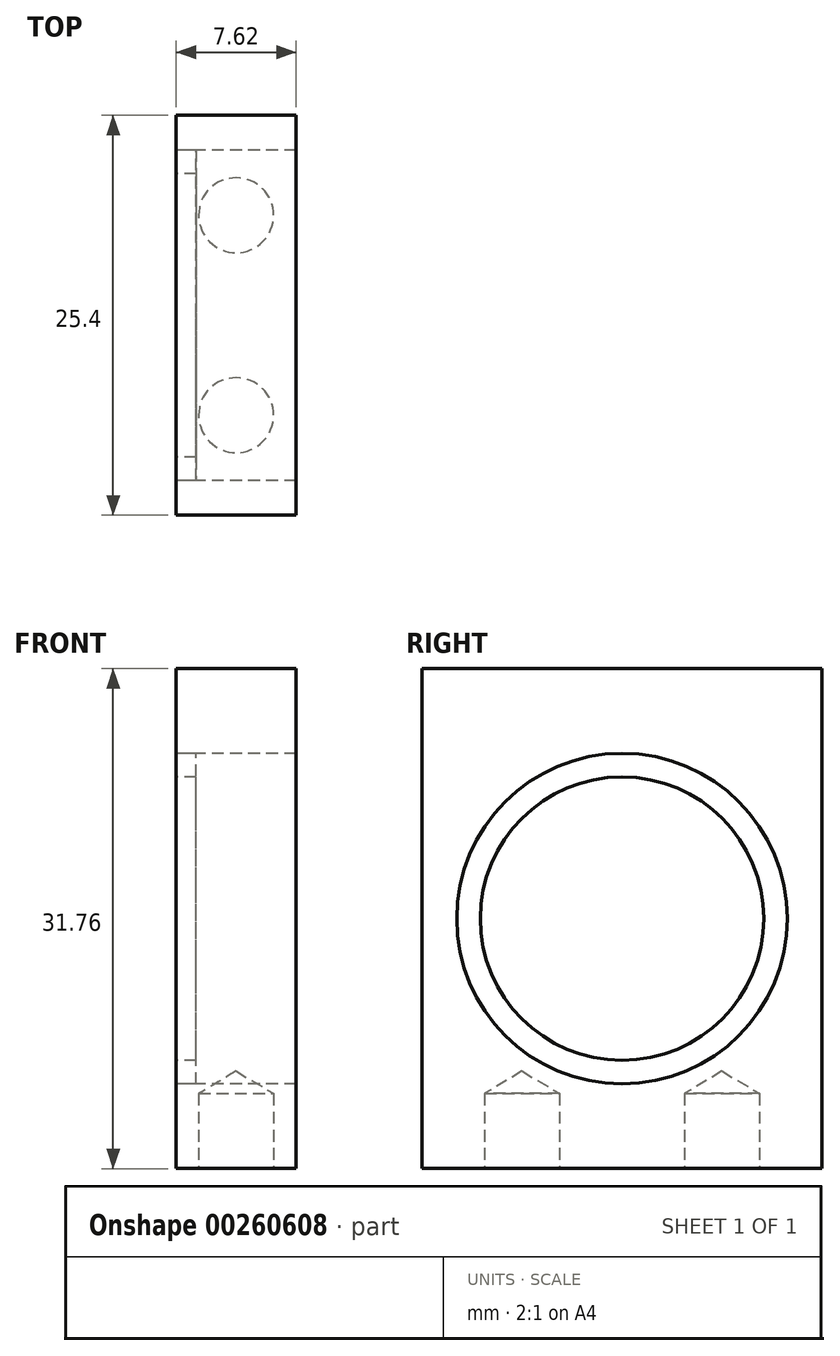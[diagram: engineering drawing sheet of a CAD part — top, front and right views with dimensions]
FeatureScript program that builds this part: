
annotation { "Feature Type Name" : "Feature", "Feature Type Description" : "" }
export const myFeature = defineFeature(function(context is Context, id is Id, definition is map)
    precondition{}
    {
        {
            var Q0;
            Q0=qCreatedBy(makeId("Right.planeOp"),FACE);
            var sketch = newSketch(context, id + "F0", { "sketchPlane" : qUnion([Q0])});
            skLineSegment(sketch, "E0.bottom", {"start": v(12.7, 15.88) * mm, "end": v(-12.7, 15.88) * mm});
            skLineSegment(sketch, "E0.top", {"start": v(12.7, -15.88) * mm, "end": v(-12.7, -15.88) * mm});
            skLineSegment(sketch, "E0.left", {"start": v(12.7, 15.88) * mm, "end": v(12.7, -15.88) * mm});
            skLineSegment(sketch, "E0.right", {"start": v(-12.7, 15.88) * mm, "end": v(-12.7, -15.88) * mm});
            skPoint(sketch, "E0.middle", {"position": v(0, 0) * mm});
            skCircle(sketch, "E1", {"center": v(0, 0) * mm, "radius": 9 * mm});
            skCircle(sketch, "E2", {"center": v(0, 0) * mm, "radius": 10.5 * mm});
            skSolve(sketch);
        }
        {
            var Q0;
            Q0=makeQuery(id+"F0.imprint","IMPRINT",FACE,{"disambiguationData":[TD([[makeQuery(id+"F0.imprint","IMPRINT",EDGE,{"derivedFrom":sQuery(id+"F0.wireOp",EDGE,"E0.bottom")}),1.0]])]});
            extrude(context, id + "F1", {"entities" : qUnion([Q0]), "depth" : 7.62 * mm});
        }
        {
            var Q0;
            Q0=makeQuery(id+"F1.opExtrude","SWEPT_FACE",FACE,{"disambiguationData":[OSD([sQuery(id+"F0.wireOp",EDGE,"E0.top")])]});
            var sketch = newSketch(context, id + "F2", { "sketchPlane" : qUnion([Q0])});
            skPoint(sketch, "E3", {"position": v(3.81, 6.35) * mm});
            skPoint(sketch, "E4", {"position": v(3.81, -6.35) * mm});
            skSolve(sketch);
        }
        {
            var Q0;
            Q0=sQuery(id+"F2.wireOp",VERTEX,"E3");
            var Q1;
            Q1=sQuery(id+"F2.wireOp",VERTEX,"2b904e9f-9de2-4966-a771-d22097fc08a8");
            var Q2;
            Q2=sQuery(id+"F2.wireOp",VERTEX,"E4");
            var Q3;
            Q3=makeQuery(id+"F1.opExtrude","SWEPT_BODY",BODY,{"disambiguationData":[OSD([sQuery(id+"F0.wireOp",EDGE,"E0.bottom"),sQuery(id+"F0.wireOp",EDGE,"E0.top"),sQuery(id+"F0.wireOp",EDGE,"E0.left"),sQuery(id+"F0.wireOp",EDGE,"E0.right"),sQuery(id+"F0.wireOp",EDGE,"E1")])]});
            hole(context, id + "F3", {"style" : HoleStyle.SIMPLE, "endStyle" : HoleEndStyle.BLIND, "holeDiameter" : 4.76 * mm, "holeDepth" : 4.76 * mm, "tappedDepth" : 12.7 * mm, "tapClearance" : 3, "locations" : qUnion([Q0, Q1, Q2]), "scope" : qUnion([Q3])});
        }
        {
            var Q0;
            Q0=makeQuery(id+"F0.imprint","IMPRINT",FACE,{"disambiguationData":[TD([[makeQuery(id+"F0.imprint","IMPRINT",EDGE,{"derivedFrom":sQuery(id+"F0.wireOp",EDGE,"E1")}),-1.0]])]});
            extrude(context, id + "F4", {"entities" : qUnion([Q0]), "depth" : 1.27 * mm});
        }
    });
